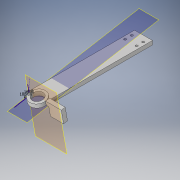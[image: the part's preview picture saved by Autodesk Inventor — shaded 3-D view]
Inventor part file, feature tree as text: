
AUTODESK INVENTOR PART (.ipt)
format: ipt  version: 2017 (Build 210142000, 142)  size: 175,616 bytes
history: native  units: in
note: dims shown in document units (in); Inventor stores cm internally (conversion verified against a paired STEP export)
features: sketch x6, projected_geometry x6, extrude x3, plane x2, hole x2
ambient origin geometry x8: Origin, YZ Plane, XZ Plane, XY Plane, X Axis, Y Axis, Z Axis, Center Point
bodies: Solid1 (feature_tree)
feature tree (19):
  extrude  "Extrusion1"  Depth=5.0in
  sketch  "Sketch2"  dims[d2=0.1875in d3=0.0in d4=0.6871in]
  plane  "Work Plane1"
  extrude  "Extrusion2"  Depth=0.1875in
  hole  "Hole2"  [1 undecoded]
  plane  "Work Plane3"
  extrude  "Extrusion3"  Depth=0.1875in TaperAngle=0.0deg
  hole  "Hole3"  [1 undecoded]
  sketch  "Sketch1"  dims[d0=0.85in d1=5.0in]
  sketch  "Sketch3"  dims[d5=0.75in d6=0.85in]
  projected_geometry  "Projected Loop1"
  projected_geometry  "Projected Loop2"
  sketch  "Sketch5"  dims[d7=0.425in d8=0.1875in d9=0.0in]
  projected_geometry  "Projected Loop4"
  sketch  "Sketch7"  dims[d17=0.51in d18=0.75in d19=0.375in d20=0.25in d21=0.5635in d22=1.0in d23=0.8108in d24=0.0687in]
  projected_geometry  "Projected Loop7"
  projected_geometry  "Projected Loop8"
  sketch  "Sketch9"  dims[d25=90.0deg d26=0.75in d27=0.625in d28=0.625in d29=0.1875in d30=0.0in d34=0.6299in d35=0.315in d36=0.1575in d37=0.85in d38=0.425in d39=0.44in d40=0.11in d41=0.75in d42=0.375in d43=0.25in d44=0.5635in d45=1.0in d46=0.8108in]
  projected_geometry  "Projected Loop10"
note: 2 required parameter values undecoded (feature->parameter linkage not recoverable at this tier; creation-order binding heuristic only, values carry confidence <= 0.55)
